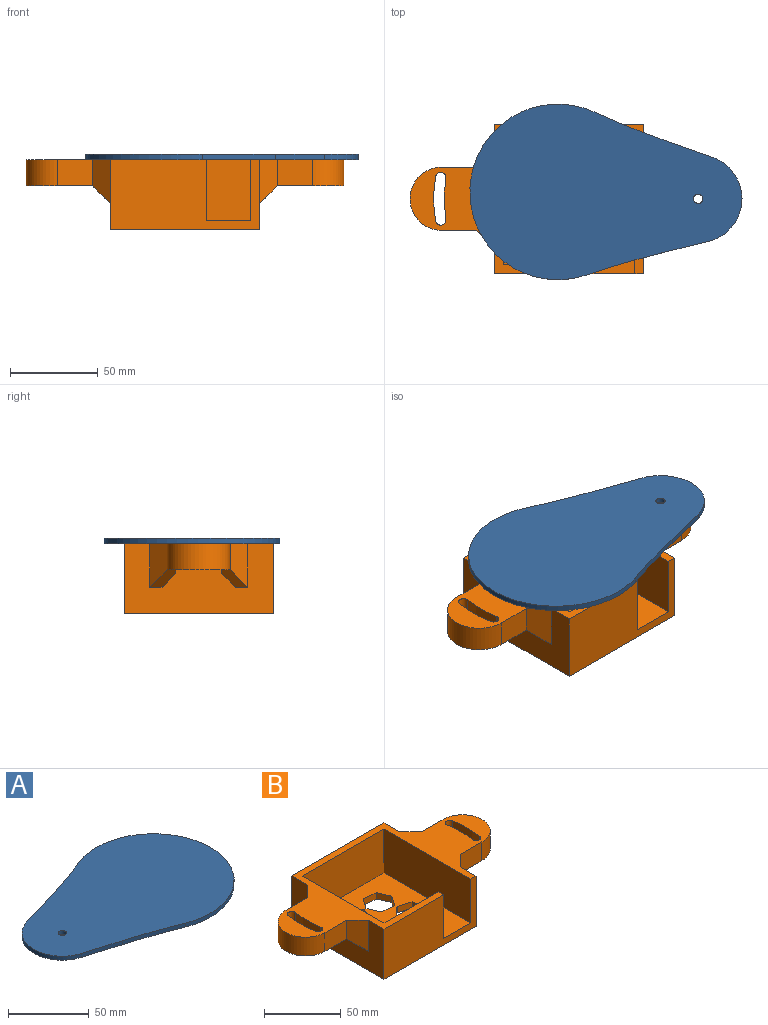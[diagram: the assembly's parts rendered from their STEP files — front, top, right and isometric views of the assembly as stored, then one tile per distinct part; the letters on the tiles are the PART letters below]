
ASSEMBLY  parts=2 mates=1
PART A: 9 faces, bbox 155x100x3 mm
  f0: plane 27.51x8.22mm, normal (-0.29,0.96,0), area 86.1mm2, adj f1,f4,f5,f7
  f1: cylinder r=25mm len=47.91mm, axis (0,0,-1), area 192.1mm2, adj f0,f2,f4,f5
  f2: plane 27.51x8.22mm, normal (-0.29,-0.96,0), area 86.1mm2, adj f1,f4,f5,f6
  f3: cylinder r=50mm len=100mm, axis (0,0,-1), area 584.5mm2, adj f4,f5,f6,f7
  f4: plane 155x100mm, normal (0,0,1), area 11092.4mm2, adj f0,f1,f2,f3,f6,f7,f8
  f5: plane 155x100mm, normal (0,0,-1), area 11092.4mm2, adj f0,f1,f2,f3,f6,f7,f8
  f6: cylinder r=500mm len=41.21mm, axis (0,0,-1), area 130.9mm2, adj f2,f3,f4,f5
  f7: cylinder r=500mm len=41.21mm, axis (0,0,-1), area 130.9mm2, adj f0,f3,f4,f5
  f8: cylinder r=2.65mm len=5.3mm, axis (0,0,-1), area 50mm2, adj f4,f5
PART B: 219 faces, bbox 181x85x40 mm
  f0: plane 85x40mm, normal (0,1,0), area 2903.3mm2, adj f5,f6,f7,f8,f90,f91,f92,f93
  f1: plane 38x36mm, normal (0,0,-1), area 669.8mm2, adj f3,f15,f16,f17,f18,f19,f20,f21
  f2: plane 38x36mm, normal (0,0,-1), area 669.8mm2, adj f4,f22,f23,f24,f25,f26,f27,f28
  f3: plane 15x10mm, normal (-0.71,0,-0.71), area 97mm2, adj f1,f6,f29,f45,f46
  f4: plane 15x10mm, normal (0.71,0,-0.71), area 97mm2, adj f2,f8,f32,f37,f38
  f5: plane 181x85mm, normal (0,0,1), area 4507mm2, adj f0,f6,f8,f9,f11,f12,f13,f14
  f6: plane 85x40mm, normal (-1,0,0), area 2837.2mm2, adj f0,f3,f5,f7,f9,f29,f30,f31
  f7: plane 85x85mm, normal (0,0,-1), area 5653.2mm2, adj f0,f6,f8,f9,f58,f59,f60,f61
  f8: plane 85x40mm, normal (1,0,0), area 2837.2mm2, adj f0,f4,f5,f7,f9,f32,f33,f34
  f9: plane 85x40mm, normal (0,-1,0), area 2525mm2, adj f5,f6,f7,f8,f10,f12,f35
  f10: plane 80x75mm, normal (0,0,1), area 4178.2mm2, adj f9,f11,f12,f13,f14,f35,f58,f59
  f11: plane 75x35mm, normal (0,-1,0), area 2625mm2, adj f5,f10,f12,f14
  f12: plane 80x35mm, normal (-1,0,0), area 2800mm2, adj f5,f9,f10,f11
  f13: plane 50x35mm, normal (0,1,0), area 1750mm2, adj f5,f10,f14,f35
  f14: plane 75x35mm, normal (1,0,0), area 2625mm2, adj f5,f10,f11,f13
  f15: plane 20x15mm, normal (0,1,0), area 300mm2, adj f1,f5,f16,f31
  f16: cylinder r=18mm len=36mm, axis (0,0,1), area 848.2mm2, adj f1,f5,f15,f21
  f17: cylinder r=3mm len=15mm, axis (0,0,1), area 141.4mm2, adj f1,f5,f18,f20
  f18: cylinder r=71mm len=23.03mm, axis (0,0,1), area 346.9mm2, adj f1,f5,f17,f19
  f19: cylinder r=3mm len=15mm, axis (0,0,1), area 141.4mm2, adj f1,f5,f18,f20
  f20: cylinder r=77mm len=24.97mm, axis (0,0,1), area 376.3mm2, adj f1,f5,f17,f19
  f21: plane 20x15mm, normal (0,-1,0), area 300mm2, adj f1,f5,f16,f29
  f22: plane 20x15mm, normal (0,-1,0), area 300mm2, adj f2,f5,f23,f34
  f23: cylinder r=18mm len=36mm, axis (0,0,1), area 848.2mm2, adj f2,f5,f22,f28
  f24: cylinder r=71mm len=23.03mm, axis (0,0,1), area 346.9mm2, adj f2,f5,f25,f27
  f25: cylinder r=3mm len=15mm, axis (0,0,1), area 141.4mm2, adj f2,f5,f24,f26
  f26: cylinder r=77mm len=24.97mm, axis (0,0,1), area 376.3mm2, adj f2,f5,f25,f27
  f27: cylinder r=3mm len=15mm, axis (0,0,1), area 141.4mm2, adj f2,f5,f24,f26
  f28: plane 20x15mm, normal (0,1,0), area 300mm2, adj f2,f5,f23,f32
  f29: plane 25x10mm, normal (-0.71,-0.71,0), area 282.8mm2, adj f3,f5,f6,f21
  f30: plane 15x10mm, normal (-0.71,0,-0.71), area 97mm2, adj f1,f6,f31,f44,f50
  f31: plane 25x10mm, normal (-0.71,0.71,0), area 282.8mm2, adj f5,f6,f15,f30
  f32: plane 25x10mm, normal (0.71,0.71,0), area 282.8mm2, adj f4,f5,f8,f28
  f33: plane 15x10mm, normal (0.71,0,-0.71), area 97mm2, adj f2,f8,f34,f36,f42
  f34: plane 25x10mm, normal (0.71,-0.71,0), area 282.8mm2, adj f5,f8,f22,f33
  f35: plane 35x5mm, normal (1,0,0), area 175mm2, adj f5,f9,f10,f13
  f36: plane 20x7.93mm, normal (-0.71,0.71,0), area 179.8mm2, adj f8,f33,f42,f43
  f37: plane 20x7.93mm, normal (-0.71,-0.71,0), area 179.8mm2, adj f4,f8,f38,f43
  f38: plane 14.65x12.07mm, normal (0,-1,0), area 148.7mm2, adj f2,f4,f37,f40,f43
  f39: cylinder r=8mm len=10mm, axis (0,0,1), area 23.1mm2, adj f2,f41,f42,f43
  f40: cylinder r=8mm len=10mm, axis (0,0,1), area 23.1mm2, adj f2,f38,f41,f43
  f41: cylinder r=66mm len=21.41mm, axis (0,0,1), area 215mm2, adj f2,f39,f40,f43
  f42: plane 14.65x12.07mm, normal (0,1,0), area 148.7mm2, adj f2,f33,f36,f39,f43
  f43: plane 41.86x23.5mm, normal (0,0,-1), area 663.3mm2, adj f8,f36,f37,f38,f39,f40,f41,f42
  f44: plane 20x7.93mm, normal (0.71,-0.71,0), area 179.8mm2, adj f6,f30,f50,f51
  f45: plane 20x7.93mm, normal (0.71,0.71,0), area 179.8mm2, adj f3,f6,f46,f51
  f46: plane 14.65x12.07mm, normal (0,1,0), area 148.7mm2, adj f1,f3,f45,f47,f51
  f47: cylinder r=8mm len=10mm, axis (0,0,1), area 23.1mm2, adj f1,f46,f48,f51
  f48: cylinder r=66mm len=21.41mm, axis (0,0,1), area 215mm2, adj f1,f47,f49,f51
  f49: cylinder r=8mm len=10mm, axis (0,0,1), area 23.1mm2, adj f1,f48,f50,f51
  f50: plane 14.65x12.07mm, normal (0,-1,0), area 148.7mm2, adj f1,f30,f44,f49,f51
  f51: plane 41.86x23.5mm, normal (0,0,-1), area 663.3mm2, adj f6,f44,f45,f46,f47,f48,f49,f50
  f52: cylinder r=82mm len=18.84mm, axis (0,0,1), area 188.9mm2, adj f2,f53,f54
  f53: cylinder r=13mm len=18.84mm, axis (0,0,1), area 210.8mm2, adj f2,f52,f54
  f54: plane 18.84x4.04mm, normal (0,0,-1), area 45.8mm2, adj f52,f53
  f55: plane 18.84x4.04mm, normal (0,0,-1), area 45.8mm2, adj f56,f57
  f56: cylinder r=13mm len=18.84mm, axis (0,0,1), area 210.8mm2, adj f1,f55,f57
  f57: cylinder r=82mm len=18.84mm, axis (0,0,1), area 188.9mm2, adj f1,f55,f56
  f58: plane 9.53x5.5mm, normal (0.5,-0.87,0), area 55mm2, adj f7,f10,f59,f63
  f59: plane 9.53x5.5mm, normal (-0.5,-0.87,0), area 55mm2, adj f7,f10,f58,f60
  f60: plane 11x5mm, normal (-1,0,0), area 55mm2, adj f7,f10,f59,f61
  f61: plane 9.53x5.5mm, normal (-0.5,0.87,0), area 55mm2, adj f7,f10,f60,f62
  f62: plane 9.53x5.5mm, normal (0.5,0.87,0), area 55mm2, adj f7,f10,f61,f63
  f63: plane 11x5mm, normal (1,0,0), area 55mm2, adj f7,f10,f58,f62
  f64: plane 10.4x5mm, normal (-0.33,0.95,0), area 55mm2, adj f7,f10,f65,f69
  f65: plane 8.3x7.22mm, normal (0.66,0.75,0), area 55mm2, adj f7,f10,f64,f66
  f66: plane 10.8x5mm, normal (0.98,-0.19,0), area 55mm2, adj f7,f10,f65,f67
  f67: plane 10.4x5mm, normal (0.33,-0.95,0), area 55mm2, adj f7,f10,f66,f68
  f68: plane 8.3x7.22mm, normal (-0.66,-0.75,0), area 55mm2, adj f7,f10,f67,f69
  f69: plane 10.8x5mm, normal (-0.98,0.19,0), area 55mm2, adj f7,f10,f64,f68
  f70: plane 8.96x6.39mm, normal (0.81,-0.58,0), area 55mm2, adj f7,f10,f71,f75
  f71: plane 10.95x5mm, normal (-0.1,-1,0), area 55mm2, adj f7,f10,f70,f72
  f72: plane 10.01x5mm, normal (-0.91,-0.41,0), area 55mm2, adj f7,f10,f71,f73
  f73: plane 8.96x6.39mm, normal (-0.81,0.58,0), area 55mm2, adj f7,f10,f72,f74
  f74: plane 10.95x5mm, normal (0.1,1,0), area 55mm2, adj f7,f10,f73,f75
  f75: plane 10.01x5mm, normal (0.91,0.41,0), area 55mm2, adj f7,f10,f70,f74
  f76: plane 10.48x5mm, normal (-0.3,-0.95,0), area 55mm2, adj f7,f10,f77,f81
  f77: plane 10.75x5mm, normal (-0.98,-0.21,0), area 55mm2, adj f7,f10,f76,f78
  f78: plane 8.14x7.4mm, normal (-0.67,0.74,0), area 55mm2, adj f7,f10,f77,f79
  f79: plane 10.48x5mm, normal (0.3,0.95,0), area 55mm2, adj f7,f10,f78,f80
  f80: plane 10.75x5mm, normal (0.98,0.21,0), area 55mm2, adj f7,f10,f79,f81
  f81: plane 8.14x7.4mm, normal (0.67,-0.74,0), area 55mm2, adj f7,f10,f76,f80
  f82: plane 8.81x6.58mm, normal (0.8,0.6,0), area 55mm2, adj f7,f10,f83,f87
  f83: plane 10.11x5mm, normal (0.92,-0.39,0), area 55mm2, adj f7,f10,f82,f84
  f84: plane 10.92x5mm, normal (0.12,-0.99,0), area 55mm2, adj f7,f10,f83,f85
  f85: plane 8.81x6.58mm, normal (-0.8,-0.6,0), area 55mm2, adj f7,f10,f84,f86
  f86: plane 10.11x5mm, normal (-0.92,0.39,0), area 55mm2, adj f7,f10,f85,f87
  f87: plane 10.92x5mm, normal (-0.12,0.99,0), area 55mm2, adj f7,f10,f82,f86
  f88: extruded ~2x1.51mm, area 3.5mm2, adj f100,f103,f105,f106
  f89: extruded ~3.07x2mm, area 6.1mm2, adj f100,f101,f105,f106
  f90: plane 9.35x2mm, normal (1,0,0), area 18.7mm2, adj f0,f91,f104,f105
  f91: plane 2x1.67mm, normal (0,0,-1), area 3.3mm2, adj f0,f90,f92,f105
  f92: plane 9.4x6.6mm, normal (-0.82,0,-0.57), area 23mm2, adj f0,f91,f93,f105
  f93: plane 2x1.38mm, normal (-1,0,0), area 2.8mm2, adj f0,f92,f94,f105
  f94: plane 6.76x2mm, normal (0,0,1), area 13.5mm2, adj f0,f93,f95,f105
  f95: plane 3.19x2mm, normal (-1,0,0), area 6.4mm2, adj f0,f94,f96,f105
  f96: plane 2x1.51mm, normal (0,0,1), area 3mm2, adj f0,f95,f97,f105
  f97: plane 3.19x2mm, normal (1,0,0), area 6.4mm2, adj f0,f96,f98,f105
  f98: plane 2.06x2mm, normal (0,0,1), area 4.1mm2, adj f0,f97,f99,f105
  f99: plane 2x1.44mm, normal (1,0,0), area 2.9mm2, adj f0,f98,f104,f105
  f100: plane 2x0.08mm, normal (0,0,1), area 0.2mm2, adj f88,f89,f105,f106
  f101: plane 4.62x2mm, normal (-1,0,0), area 9.2mm2, adj f89,f102,f105,f106
  f102: plane 5.18x2mm, normal (0,0,-1), area 10.4mm2, adj f101,f103,f105,f106
  f103: plane 6.18x4.34mm, normal (0.82,0,0.58), area 15.1mm2, adj f88,f102,f105,f106
  f104: plane 2.06x2mm, normal (0,0,-1), area 4.1mm2, adj f0,f90,f99,f105
  f105: plane 13.98x10.33mm, normal (0,1,0), area 46.7mm2, adj f88,f89,f90,f91,f92,f93,f94,f95
  f106: plane 7.69x5.28mm, normal (0,1,0), area 19.3mm2, adj f88,f89,f100,f101,f102,f103
  f107: extruded ~2.42x2mm, area 4.9mm2, adj f0,f108,f123,f126
  f108: extruded ~3.56x2.91mm, area 10.5mm2, adj f0,f107,f109,f126
  f109: extruded ~2.28x2mm, area 5.1mm2, adj f0,f108,f110,f126
  f110: extruded ~2.6x2mm, area 5.5mm2, adj f0,f109,f111,f126
  f111: extruded ~2x1.95mm, area 3.9mm2, adj f0,f110,f112,f126
  f112: extruded ~2x1.65mm, area 3.6mm2, adj f0,f111,f124,f126
  f113: extruded ~3.58x2mm, area 7.4mm2, adj f0,f114,f124,f126
  f114: extruded ~3.79x2mm, area 8.1mm2, adj f0,f113,f115,f126
  f115: extruded ~3.38x2mm, area 7.5mm2, adj f0,f114,f116,f126
  f116: extruded ~2.98x2mm, area 6.7mm2, adj f0,f115,f117,f126
  f117: extruded ~3.46x2mm, area 7.4mm2, adj f0,f116,f118,f126
  f118: extruded ~2.18x2mm, area 4.4mm2, adj f0,f117,f125,f126
  f119: plane 5.56x2mm, normal (0,0,1), area 11.1mm2, adj f0,f120,f125,f126
  f120: plane 2x1.45mm, normal (1,0,0), area 2.9mm2, adj f0,f119,f121,f126
  f121: plane 6.91x2mm, normal (0,0,-1), area 13.8mm2, adj f0,f120,f122,f126
  f122: plane 6.5x2mm, normal (-1,0,-0.08), area 13mm2, adj f0,f121,f123,f126
  f123: plane 2x0.82mm, normal (-0.54,0,0.84), area 1.9mm2, adj f0,f107,f122,f126
  f124: plane 2x1.52mm, normal (-1,0,0), area 3mm2, adj f0,f112,f113,f126
  f125: plane 4.17x2mm, normal (1,0,0.08), area 8.4mm2, adj f0,f118,f119,f126
  f126: plane 14.09x8.75mm, normal (0,1,0), area 44.8mm2, adj f107,f108,f109,f110,f111,f112,f113,f114
  f127: plane 2x1.27mm, normal (1,0,0), area 2.5mm2, adj f0,f128,f133,f134
  f128: plane 9.25x2mm, normal (0,0,-1), area 18.5mm2, adj f0,f127,f129,f134
  f129: plane 2x1.45mm, normal (-1,0,0), area 2.9mm2, adj f0,f128,f130,f134
  f130: plane 7.57x2mm, normal (0,0,1), area 15.1mm2, adj f0,f129,f131,f134
  f131: plane 12.45x5.76mm, normal (-0.91,0,-0.42), area 27.4mm2, adj f0,f130,f132,f134
  f132: plane 2x1.75mm, normal (0,0,1), area 3.5mm2, adj f0,f131,f133,f134
  f133: plane 12.63x5.68mm, normal (0.91,0,0.41), area 27.7mm2, adj f0,f127,f132,f134
  f134: plane 13.9x9.25mm, normal (0,1,0), area 34.2mm2, adj f127,f128,f129,f130,f131,f132,f133
  f135: extruded ~2.48x2mm, area 5.2mm2, adj f0,f136,f158,f161
  f136: extruded ~3.19x2mm, area 7.1mm2, adj f0,f135,f137,f161
  f137: extruded ~3.42x2mm, area 7.4mm2, adj f0,f136,f138,f161
  f138: extruded ~3.08x2mm, area 6.7mm2, adj f0,f137,f139,f161
  f139: extruded ~2.93x2mm, area 6.4mm2, adj f0,f138,f140,f161
  f140: extruded ~2x1.95mm, area 4mm2, adj f0,f139,f141,f161
  f141: extruded ~2x1.39mm, area 3.7mm2, adj f0,f140,f159,f161
  f142: extruded ~4.33x2mm, area 9.2mm2, adj f0,f143,f159,f161
  f143: extruded ~3.45x2mm, area 7.7mm2, adj f0,f142,f144,f161
  f144: extruded ~2x1.73mm, area 3.5mm2, adj f0,f143,f160,f161
  f145: extruded ~2x1.75mm, area 3.5mm2, adj f0,f146,f160,f161
  f146: extruded ~8.16x6.31mm, area 23.6mm2, adj f0,f145,f147,f161
  f147: extruded ~3.28x2mm, area 6.7mm2, adj f0,f146,f158,f161
  f148: extruded ~2x1.84mm, area 3.8mm2, adj f149,f157,f161,f162
  f149: extruded ~2x1.27mm, area 2.7mm2, adj f148,f150,f161,f162
  f150: extruded ~2x1.15mm, area 3mm2, adj f149,f151,f161,f162
  f151: extruded ~2x1.59mm, area 3.3mm2, adj f150,f152,f161,f162
  f152: extruded ~2.08x2mm, area 4.6mm2, adj f151,f153,f161,f162
  f153: extruded ~2.15x2mm, area 4.6mm2, adj f152,f154,f161,f162
  f154: extruded ~2.44x2mm, area 5.2mm2, adj f153,f155,f161,f162
  f155: extruded ~2.1x2mm, area 4.7mm2, adj f154,f156,f161,f162
  f156: extruded ~2x1.6mm, area 3.4mm2, adj f155,f157,f161,f162
  f157: extruded ~2x1.33mm, area 3.5mm2, adj f148,f156,f161,f162
  f158: extruded ~2.12x2mm, area 5.4mm2, adj f0,f135,f147,f161
  f159: plane 2x0.11mm, normal (0,0,1), area 0.2mm2, adj f0,f141,f142,f161
  f160: plane 2x1.36mm, normal (-1,0,0), area 2.7mm2, adj f0,f144,f145,f161
  f161: plane 14.29x9.08mm, normal (0,1,0), area 50.1mm2, adj f135,f136,f137,f138,f139,f140,f141,f142
  f162: plane 6.25x5.92mm, normal (0,1,0), area 29.8mm2, adj f148,f149,f150,f151,f152,f153,f154,f155
  f163: extruded ~2.26x2mm, area 5.8mm2, adj f0,f164,f167,f172
  f164: extruded ~2x0.45mm, area 1.2mm2, adj f0,f163,f165,f172
  f165: extruded ~2.34x2mm, area 4.7mm2, adj f0,f164,f168,f172
  f166: plane 3.68x2.84mm, normal (-0.61,0,-0.79), area 9.3mm2, adj f0,f167,f171,f172
  f167: plane 2x1.08mm, normal (-0.79,0,0.61), area 2.7mm2, adj f0,f163,f166,f172
  f168: plane 9.91x2mm, normal (-1,0,0), area 19.8mm2, adj f0,f165,f169,f172
  f169: plane 2x1.54mm, normal (0,0,1), area 3.1mm2, adj f0,f168,f170,f172
  f170: plane 13.9x2mm, normal (1,0,0), area 27.8mm2, adj f0,f169,f171,f172
  f171: plane 2x1.33mm, normal (0,0,-1), area 2.7mm2, adj f0,f166,f170,f172
  f172: plane 13.9x5.01mm, normal (0,1,0), area 26.4mm2, adj f163,f164,f165,f166,f167,f168,f169,f170
  f173: extruded ~3.45x2mm, area 8.1mm2, adj f0,f174,f188,f189
  f174: extruded ~5.39x2mm, area 11.2mm2, adj f0,f173,f175,f189
  f175: extruded ~5.34x2mm, area 11.1mm2, adj f0,f174,f176,f189
  f176: extruded ~3.41x2mm, area 8.1mm2, adj f0,f175,f177,f189
  f177: extruded ~3.48x2mm, area 8.2mm2, adj f0,f176,f178,f189
  f178: extruded ~5.38x2mm, area 11.1mm2, adj f0,f177,f179,f189
  f179: extruded ~5.31x2mm, area 11mm2, adj f0,f178,f188,f189
  f180: extruded ~2.29x2mm, area 5.7mm2, adj f181,f187,f189,f190
  f181: extruded ~4.39x2mm, area 9mm2, adj f180,f182,f189,f190
  f182: extruded ~4.4x2mm, area 9mm2, adj f181,f183,f189,f190
  f183: extruded ~2.29x2mm, area 5.7mm2, adj f182,f184,f189,f190
  f184: extruded ~2.27x2mm, area 5.6mm2, adj f183,f185,f189,f190
  f185: extruded ~4.42x2mm, area 9mm2, adj f184,f186,f189,f190
  f186: extruded ~4.41x2mm, area 9mm2, adj f185,f187,f189,f190
  f187: extruded ~2.27x2mm, area 5.6mm2, adj f180,f186,f189,f190
  f188: extruded ~3.44x2mm, area 8.2mm2, adj f0,f173,f179,f189
  f189: plane 14.31x9.19mm, normal (0,1,0), area 51mm2, adj f173,f174,f175,f176,f177,f178,f179,f180
  f190: plane 11.58x5.98mm, normal (0,1,0), area 58.5mm2, adj f180,f181,f182,f183,f184,f185,f186,f187
  f191: extruded ~2.26x2mm, area 5.8mm2, adj f0,f192,f195,f200
  f192: extruded ~2x0.45mm, area 1.2mm2, adj f0,f191,f193,f200
  f193: extruded ~2.34x2mm, area 4.7mm2, adj f0,f192,f196,f200
  f194: plane 3.68x2.84mm, normal (-0.61,0,-0.79), area 9.3mm2, adj f0,f195,f199,f200
  f195: plane 2x1.08mm, normal (-0.79,0,0.61), area 2.7mm2, adj f0,f191,f194,f200
  f196: plane 9.91x2mm, normal (-1,0,0), area 19.8mm2, adj f0,f193,f197,f200
  f197: plane 2x1.54mm, normal (0,0,1), area 3.1mm2, adj f0,f196,f198,f200
  f198: plane 13.9x2mm, normal (1,0,0), area 27.8mm2, adj f0,f197,f199,f200
  f199: plane 2x1.33mm, normal (0,0,-1), area 2.7mm2, adj f0,f194,f198,f200
  f200: plane 13.9x5.01mm, normal (0,1,0), area 26.4mm2, adj f191,f192,f193,f194,f195,f196,f197,f198
  f201: extruded ~3.45x2mm, area 8.1mm2, adj f0,f202,f216,f217
  f202: extruded ~5.39x2mm, area 11.2mm2, adj f0,f201,f203,f217
  f203: extruded ~5.34x2mm, area 11.1mm2, adj f0,f202,f204,f217
  f204: extruded ~3.41x2mm, area 8.1mm2, adj f0,f203,f205,f217
  f205: extruded ~3.48x2mm, area 8.2mm2, adj f0,f204,f206,f217
  f206: extruded ~5.38x2mm, area 11.1mm2, adj f0,f205,f207,f217
  f207: extruded ~5.31x2mm, area 11mm2, adj f0,f206,f216,f217
  f208: extruded ~2.29x2mm, area 5.7mm2, adj f209,f215,f217,f218
  f209: extruded ~4.39x2mm, area 9mm2, adj f208,f210,f217,f218
  f210: extruded ~4.4x2mm, area 9mm2, adj f209,f211,f217,f218
  f211: extruded ~2.29x2mm, area 5.7mm2, adj f210,f212,f217,f218
  f212: extruded ~2.27x2mm, area 5.6mm2, adj f211,f213,f217,f218
  f213: extruded ~4.42x2mm, area 9mm2, adj f212,f214,f217,f218
  f214: extruded ~4.41x2mm, area 9mm2, adj f213,f215,f217,f218
  f215: extruded ~2.27x2mm, area 5.6mm2, adj f208,f214,f217,f218
  f216: extruded ~3.44x2mm, area 8.2mm2, adj f0,f201,f207,f217
  f217: plane 14.31x9.19mm, normal (0,1,0), area 51mm2, adj f201,f202,f203,f204,f205,f206,f207,f208
  f218: plane 11.58x5.98mm, normal (0,1,0), area 58.5mm2, adj f208,f209,f210,f211,f212,f213,f214,f215
PLACE A rot(axis=(0,0,1),177.2deg) t=(-5.5,5.21,1.28)mm
PLACE B t=(0.92,1.32,1.28)mm fixed
MATE revolute A.f1 <-> B.f5  axis (0,0,-1) through (74.4,1.32,1.28)mm
